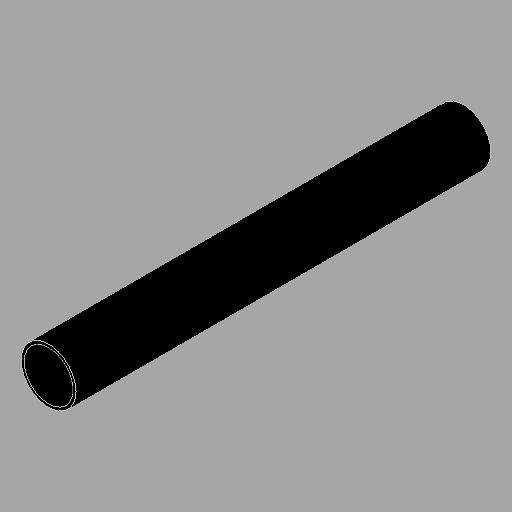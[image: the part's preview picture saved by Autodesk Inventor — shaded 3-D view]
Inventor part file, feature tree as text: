
AUTODESK INVENTOR PART (.ipt)
format: ipt  version: 2025 (Build 290162000, 162)  size: 78,848 bytes
history: native  units: in
note: dims shown in document units (in); Inventor stores cm internally (conversion verified against a paired STEP export)
features: other x3, sketch x1
ambient origin geometry x8: Origin, YZ Plane, XZ Plane, XY Plane, X Axis, Y Axis, Z Axis, Center Point
bodies: Solid1 (feature_tree)
feature tree (4):
  other  "WingBoomReinforcment.ipt"
  other  "Solid1::WingBoomReinforcment.ipt"
  other  "TaggingFeature1"
  sketch  "Sketch1"  dims[d0=0.3937in]
